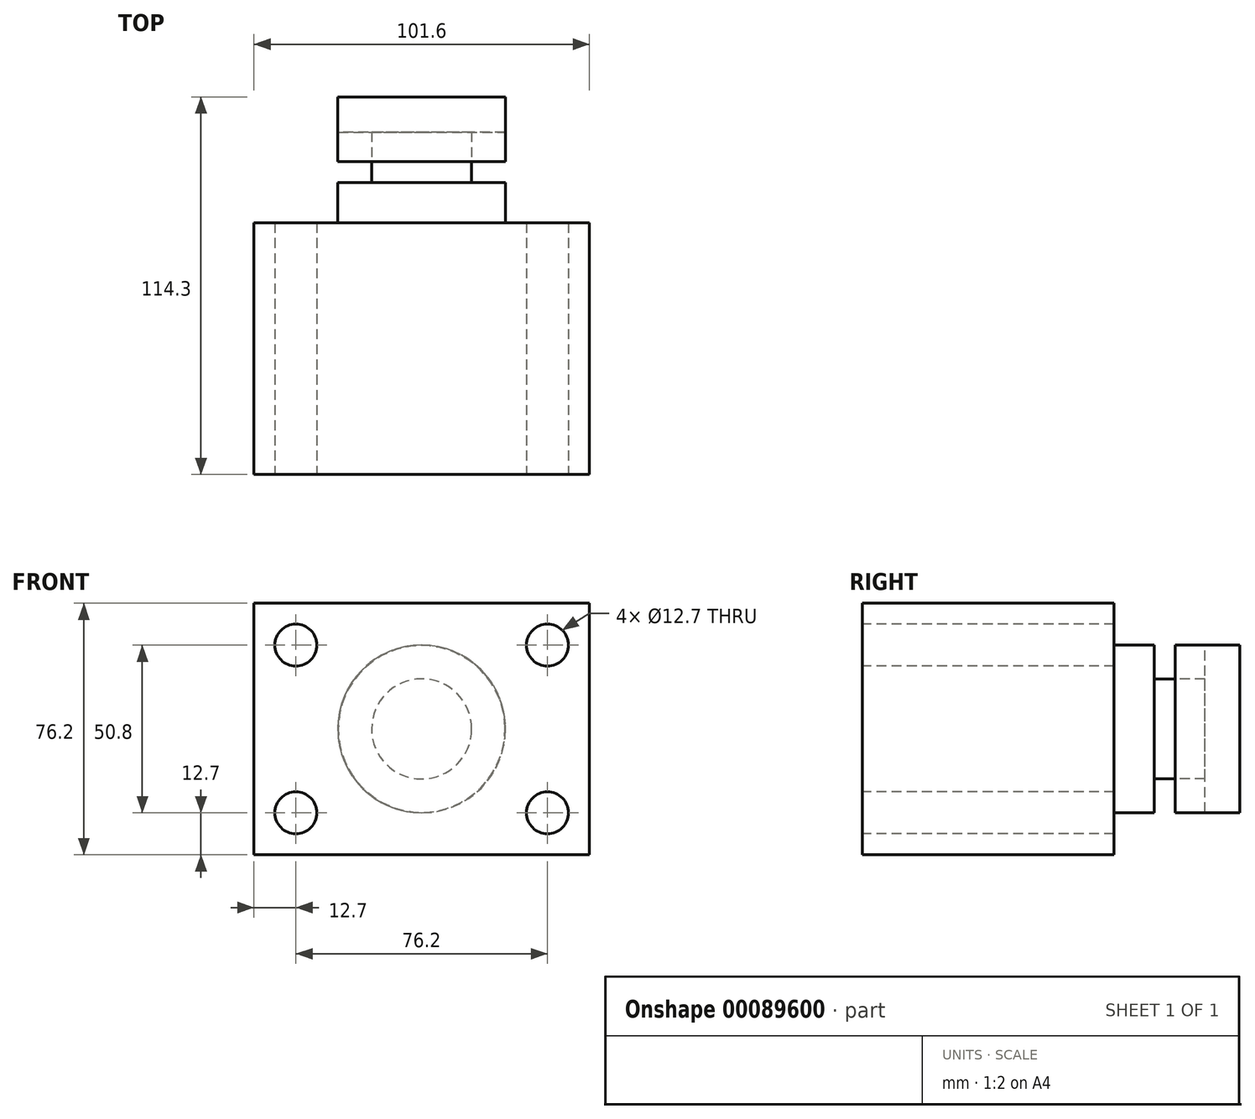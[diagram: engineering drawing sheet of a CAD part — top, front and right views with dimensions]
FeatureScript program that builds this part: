
annotation { "Feature Type Name" : "Feature", "Feature Type Description" : "" }
export const myFeature = defineFeature(function(context is Context, id is Id, definition is map)
    precondition{}
    {
        {
            var Q0;
            Q0=qCreatedBy(makeId("Front.planeOp"),FACE);
            var sketch = newSketch(context, id + "F0", { "sketchPlane" : qUnion([Q0])});
            skLineSegment(sketch, "E0", {"start": v(-50.8, 38.1) * mm, "end": v(50.8, 38.1) * mm});
            skLineSegment(sketch, "E1", {"start": v(50.8, 38.1) * mm, "end": v(50.8, -38.1) * mm});
            skLineSegment(sketch, "E2", {"start": v(50.8, -38.1) * mm, "end": v(-50.8, -38.1) * mm});
            skLineSegment(sketch, "E3", {"start": v(-50.8, -38.1) * mm, "end": v(-50.8, 38.1) * mm});
            skSolve(sketch);
        }
        {
            var Q0;
            Q0=makeQuery(id+"F0.imprint","IMPRINT",FACE,{"disambiguationData":[TD([[makeQuery(id+"F0.imprint","IMPRINT",EDGE,{"derivedFrom":sQuery(id+"F0.wireOp",EDGE,"E0")}),-1.0]])]});
            extrude(context, id + "F1", {"entities" : qUnion([Q0]), "depth" : 76.2 * mm});
        }
        {
            var Q0;
            Q0=makeQuery(id+"F1.opExtrude","CAP_FACE",FACE,{"disambiguationData":[OSD([sQuery(id+"F0.wireOp",EDGE,"E0"),sQuery(id+"F0.wireOp",EDGE,"E1"),sQuery(id+"F0.wireOp",EDGE,"E2"),sQuery(id+"F0.wireOp",EDGE,"E3")])],"isStart":false});
            var sketch = newSketch(context, id + "F2", { "sketchPlane" : qUnion([Q0])});
            skCircle(sketch, "E4", {"center": v(-38.1, 25.4) * mm, "radius": 6.35 * mm});
            skCircle(sketch, "E5", {"center": v(-38.1, -25.4) * mm, "radius": 6.35 * mm});
            skLineSegment(sketch, "E6", {"start": v(0, 46.83) * mm, "end": v(0, -51.14) * mm, "construction": true});
            skPoint(sketch, "E6.endSnap0", {"position": v(0, -38.1) * mm});
            skCircle(sketch, "E7.MirrorC", {"center": v(38.1, 25.4) * mm, "radius": 6.35 * mm});
            skCircle(sketch, "E8.MirrorC", {"center": v(38.1, -25.4) * mm, "radius": 6.35 * mm});
            skSolve(sketch);
        }
        {
            var Q0;
            Q0 = qSketchRegion(id + "F2", true);
            extrude(context, id + "F3", {"entities" : qUnion([Q0]), "operationType" : NewBodyOperationType.REMOVE, "endBound" : BoundingType.THROUGH_ALL, "oppositeDirection" : true, "depth" : 25.4 * mm});
        }
        {
            var Q0;
            Q0=qCreatedBy(makeId("Top.planeOp"),FACE);
            var sketch = newSketch(context, id + "F4", { "sketchPlane" : qUnion([Q0])});
            skLineSegment(sketch, "E9.bottom", {"start": v(-25.4, 38.1) * mm, "end": v(0, 38.1) * mm});
            skLineSegment(sketch, "E9.top", {"start": v(-25.4, 0) * mm, "end": v(0, 0) * mm});
            skLineSegment(sketch, "E9.left", {"start": v(-25.4, 38.1) * mm, "end": v(-25.4, 0) * mm});
            skLineSegment(sketch, "E9.right", {"start": v(0, 38.1) * mm, "end": v(0, 0) * mm});
            skSolve(sketch);
        }
        {
            var Q0;
            Q0 = qSketchRegion(id + "F4", true);
            var Q1;
            Q1=sQuery(id+"F4.wireOp",EDGE,"E9.right");
            revolve(context, id + "F5", {"operationType" : NewBodyOperationType.ADD, "entities" : qUnion([Q0]), "axis" : qUnion([Q1]), "revolveType" : RevolveType.FULL});
        }
        {
            var Q0;
            Q0=qCreatedBy(makeId("Right.planeOp"),FACE);
            var sketch = newSketch(context, id + "F6", { "sketchPlane" : qUnion([Q0])});
            skLineSegment(sketch, "E10", {"start": v(37.88, 0) * mm, "end": v(-76.19, 0) * mm, "construction": true});
            skLineSegment(sketch, "E11", {"start": v(27.48, -25.24) * mm, "end": v(27.48, -15.15) * mm});
            skLineSegment(sketch, "E12", {"start": v(27.48, -15.15) * mm, "end": v(12.17, -15.15) * mm});
            skLineSegment(sketch, "E13", {"start": v(12.17, -15.15) * mm, "end": v(12.17, -25.51) * mm});
            skLineSegment(sketch, "E14", {"start": v(27.48, -25.24) * mm, "end": v(12.17, -25.51) * mm});
            skSolve(sketch);
        }
        {
            var Q0;
            Q0 = qSketchRegion(id + "F6", true);
            var Q1;
            Q1=sQuery(id+"F6.wireOp",EDGE,"E10");
            revolve(context, id + "F7", {"operationType" : NewBodyOperationType.REMOVE, "entities" : qUnion([Q0]), "axis" : qUnion([Q1]), "revolveType" : RevolveType.FULL, "oppositeDirection" : true});
        }
    });
